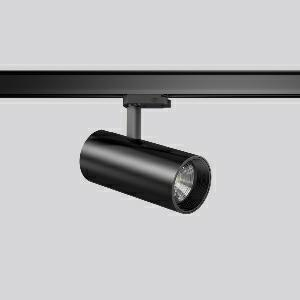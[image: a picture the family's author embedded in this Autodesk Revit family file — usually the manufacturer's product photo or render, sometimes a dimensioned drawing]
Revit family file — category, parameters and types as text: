
# Revit family: deecos_s_mini_742206_003_76_5293
name_source: partatom
category: Lighting Fixtures
units: mm (PartAtom-declared; Revit-internal decimal feet)

## family parameters
Cut with Voids When Loaded = No
Host = Face
Light Source = No
Part Type = Normal
Room Calculation Point = No
Round Connector Dimension = Use Diameter
Shared = No

## types (1)
- DEECOS S mini (1 x LED Modul 930, 3150 lm, 3000)
    Apparent Load = 29 VA
    Approval mark = CE
    CIE Flux Codes = 99 100 100 100 100
    Color Rendering = 90
    Color Temperature = 3000
    Default Elevation = 1800 mm
    Description = Series: DEECOS S mini
LED surface-mounted projector in modern design with no visible cooling ribs. Housing: die-cast aluminium, powder-coated. Rotation range: 356°. Swivel range: 90°. Black plastic ring and recessed LED to prevent glare from the side. Optical assembly with lens made of plastic (polycarbonate) for the best homogeneous light distribution - can be changed without tools. Best colour rendering index Ra>90. With adapter for RZB 3-circuit DALI tracks. Suitable for Track on ceiling, Wall track. High quality converter without flickering and stroboscopic effect. The following accessories can be mounted without use of tools: interchangeable lenses, decorative glasses, honeycomb louvre, clear and frosted diffusers, white interchangeable plastic ring. 
Colour: deep black, matt (RAL 9005)
Diameter: 87 mm
Height: 214 mm
Lamp: LED
Socket: without socket
Colour temperature: 3000K
Colour rendering index (CRI): 92
System power: 29 W
Rated luminous flux: 3150 lm
Luminous efficiency: 109 lm/W
Control gear: Converter, dimmable, DALI
Protection class: I
Type of protection: IP 20
    Height = 214 mm
    Lamp = 1 x LED Modul 930
    Lamp Light Flux = 3150 lm
    Lamp count = 1
    Length = 87 mm
    Lifetime = 50000 h
    Luminous efficacy = 109 lm/W
    Manufacturer = RZB
    ModVariant = No
    Model = 742206.003.76
    Mounting Place = Ceiling
    Mounting Type = Rail mounted
    Number of Poles = 1
    OnlyDefault = Yes
    Power Factor = 1
    Product Name = DEECOS S mini
    Product group = Track mounted projectors
    ProductGroupID = 301
    Protection Class = Protection class I
    Protection Degree = IP 20
    RLX_Detail_Level = 1
    RLX_Emergency_Light_Flux = 0 lm
    RLX_Emergency_Type = 0
    RLX_Emergency_Type_DB = No
    RlxData = <blob elided: 38969 chars, md5=3dbd1084>
    Socket = socket
    Standby Power = 0 W
    System Light Flux = 3150 lm
    System Power = 29 W
    Type Comments = Product without accessories
    Type Image = 741930.003.jpg
    URL = http://relux.com
    VarID = ---
    Voltage = 230 V
    Voltage Range = 220-240 V
    Weight = 0.00 kg
    Width = 0 mm  [stored 0 ft]

note: [stored X ft] marks values corroborated as IEEE doubles in the binary element streams (Revit-internal decimal feet)

## geometry (parser evidence)
native form markers: Blend x4, Sweep x13
no freeform markers — native parametric forms only
